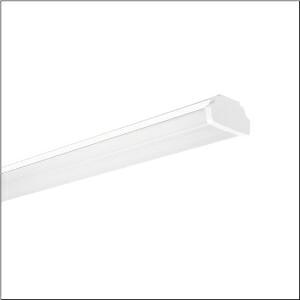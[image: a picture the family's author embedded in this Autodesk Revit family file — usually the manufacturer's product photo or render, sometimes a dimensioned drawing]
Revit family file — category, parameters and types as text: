
# Revit family: modario_r__31_gen_2_53bm812cv4dxd2_fc20
name_source: partatom
category: Lighting Fixtures
units: mm (PartAtom-declared; Revit-internal decimal feet)

## family parameters
Cut with Voids When Loaded = No
Host = Face
Light Source = No
Part Type = Normal
Room Calculation Point = No
Round Connector Dimension = Use Diameter
Shared = No

## types (1)
- --- (1 x LED, 13040 lm, 68.5 W, 4000K)
    Apparent Load = 69 VA
    CIE Flux Codes = 47 80 95 93 100
    Color Rendering = 80
    Color Temperature = 4000K
    Default Elevation = 1800 mm
    Description = Modario® 31 Gen.2, luminaire insert, of sheet steel, coil coated, white, length: 1.495mm, width: 81mm, height: 82mm, 5x system unit, system units: 299mm, LED rated luminous flux: 13.040lm, light colour: 840, control gear: ON/OFF Multilumen, CLOi, with plug, 3-pole, with phase selection, mains connection: 220..240V, AC, 50/60Hz, start of lifetime: 69W, end of service life: 82W, through-wiring accessed according to module size, primary optical cover: cover, of PMMA, light emission: direct distribution, primary light characteristic: symmetric, protection rating (complete): IP20, protection rating (LED compartment): IP50, insulation class (complete): insulation class I (protective earthing), certification: CE, ENEC, VDE, UKCA, impact resistance: IK03, permissible ambient temperature for indoor applications: -35..+35°C, corresponds to IFS (International Featured Standards) requirements for safety and quality in the food industry, reducing of maximum allowable ambient temperature of 5°C with ceiling mounting, IP40 when using the optional accessory 5TP9018, packaging unit: 1 piece
    Height = 92 mm
    Lamp = 1 x LED
    Lamp Light Flux = 13040 lm
    Lamp Power = 68.5 W
    Lamp count = 1
    Length = 1495 mm
    Luminous efficacy = 190 lm/W
    Manufacturer = Siteco
    ModVariant = No
    Model = 53BM812CV4DXD2
    Mounting Place = Ceiling
    Mounting Type = Pendant
    Number of Poles = 1
    OnlyDefault = Yes
    Power Factor = 1
    Product Name = Modario® 31 Gen.2
    Product group = luminaire insert
    ProductGroupID = 901
    Protection Class = Protection class I
    Protection Degree = IP 20
    RLX_Detail_Level = 1
    RLX_Emergency_Light_Flux = 0 lm
    RLX_Emergency_Type = 0
    RLX_Emergency_Type_DB = No
    RlxData = <blob elided: 40105 chars, md5=abc5512c>
    Socket = socket
    Standby Power = 0 W
    System Light Flux = 13040 lm
    System Power = 69 W
    Type Comments = factory setting: luminous flux: 100 % | (A | C | E) | 161 mA
    Type Image = l_1319597.jpg
    URL = http://relux.com
    VarID = @adj_010617
    Voltage = 0 V
    Weight = 0.00 kg
    Width = 81 mm

## geometry (parser evidence)
native form markers: Blend x4, Sweep x14
no freeform markers — native parametric forms only
